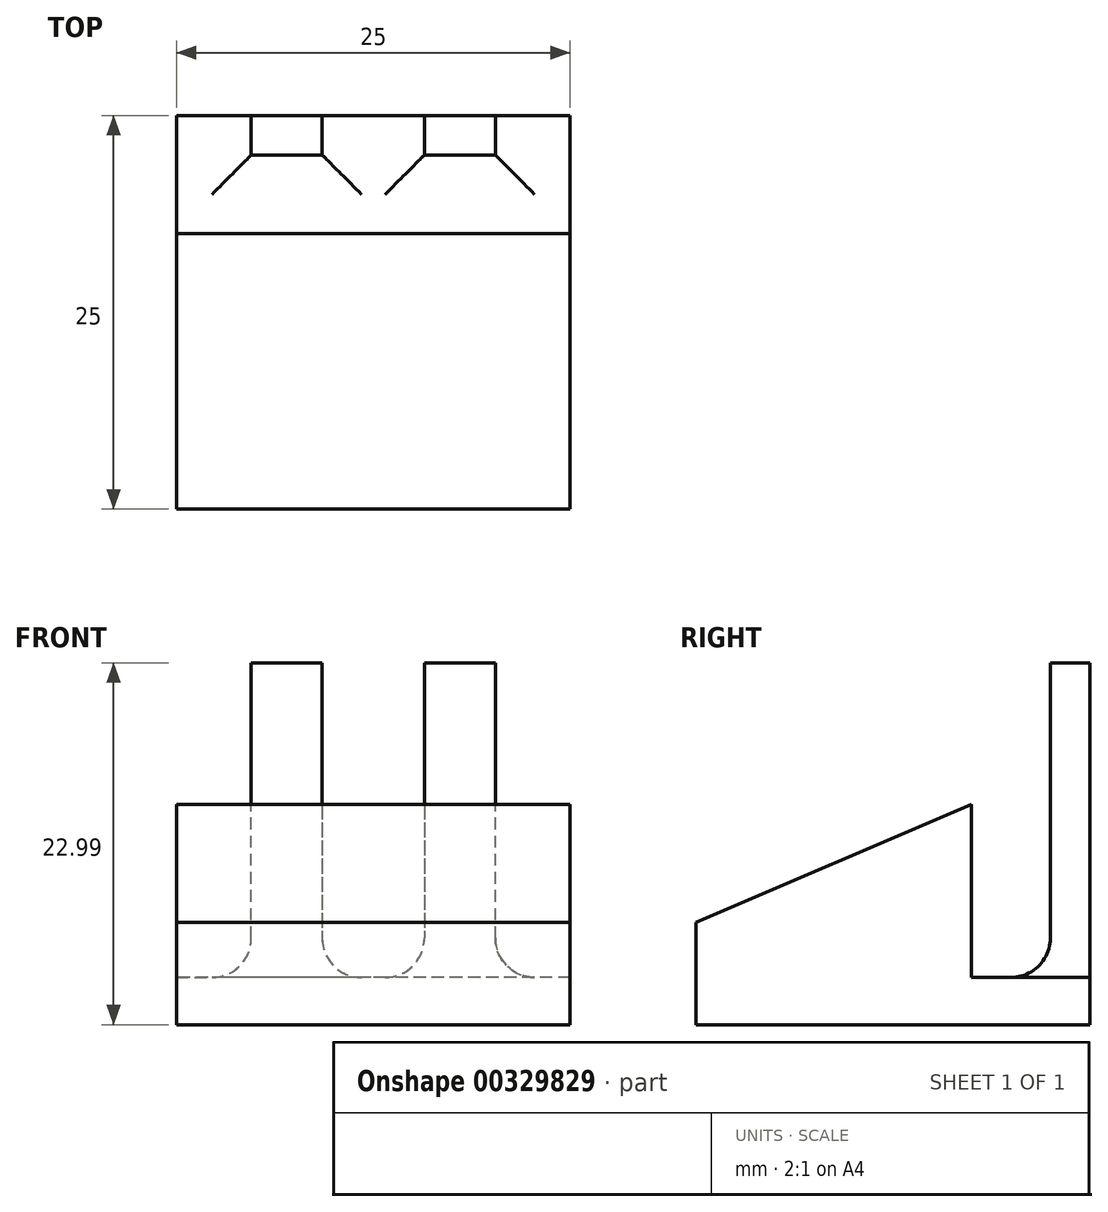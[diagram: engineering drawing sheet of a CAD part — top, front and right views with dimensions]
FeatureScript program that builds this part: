
annotation { "Feature Type Name" : "Feature", "Feature Type Description" : "" }
export const myFeature = defineFeature(function(context is Context, id is Id, definition is map)
    precondition{}
    {
        {
            var Q0;
            Q0=qCreatedBy(makeId("Right.planeOp"),FACE);
            var sketch = newSketch(context, id + "F0", { "sketchPlane" : qUnion([Q0])});
            skLineSegment(sketch, "E0", {"start": v(0, 23) * mm, "end": v(0, 0) * mm});
            skLineSegment(sketch, "E1", {"start": v(0, 0) * mm, "end": v(0, 0) * mm});
            skLineSegment(sketch, "E2", {"start": v(-25, 0) * mm, "end": v(-25, 0) * mm});
            skLineSegment(sketch, "E3", {"start": v(-25, 0) * mm, "end": v(-25, 6.5) * mm});
            skLineSegment(sketch, "E4", {"start": v(-25, 6.5) * mm, "end": v(-7.5, 14) * mm});
            skLineSegment(sketch, "E5", {"start": v(-7.5, 14) * mm, "end": v(-7.5, 14) * mm});
            skLineSegment(sketch, "E6", {"start": v(-7.5, 3) * mm, "end": v(-7.5, 3) * mm});
            skLineSegment(sketch, "E7", {"start": v(-7.5, 3) * mm, "end": v(-7.5, 14) * mm});
            skLineSegment(sketch, "E8", {"start": v(-7.5, 3) * mm, "end": v(-2.5, 3) * mm});
            skLineSegment(sketch, "E9", {"start": v(-2.5, 3) * mm, "end": v(-2.5, 3) * mm});
            skLineSegment(sketch, "E10", {"start": v(-2.5, 3) * mm, "end": v(-2.5, 23) * mm});
            skLineSegment(sketch, "E11", {"start": v(-2.5, 23) * mm, "end": v(-2.5, 23) * mm});
            skLineSegment(sketch, "E12", {"start": v(-2.5, 23) * mm, "end": v(0, 23) * mm});
            skLineSegment(sketch, "E13", {"start": v(-25, 0) * mm, "end": v(0, 0) * mm});
            skLineSegment(sketch, "E14", {"start": v(0, 60) * mm, "end": v(-140, 0) * mm, "construction": true});
            skSolve(sketch);
        }
        {
            var Q0;
            Q0 = qSketchRegion(id + "F0", true);
            extrude(context, id + "F1", {"entities" : qUnion([Q0]), "depth" : 25 * mm});
        }
        {
            var Q0;
            Q0=makeQuery(id+"F1.opExtrude","SWEPT_FACE",FACE,{"disambiguationData":[OSD([sQuery(id+"F0.wireOp",EDGE,"E0")])]});
            var sketch = newSketch(context, id + "F2", { "sketchPlane" : qUnion([Q0])});
            skLineSegment(sketch, "E15", {"start": v(-25, 3) * mm, "end": v(-20.25, 3) * mm});
            skLineSegment(sketch, "E16", {"start": v(-20.25, 3) * mm, "end": v(-20.25, 22.99) * mm});
            skLineSegment(sketch, "E17", {"start": v(-20.25, 22.99) * mm, "end": v(-15.75, 22.99) * mm});
            skLineSegment(sketch, "E18", {"start": v(-15.75, 22.99) * mm, "end": v(-15.75, 3) * mm});
            skLineSegment(sketch, "E19", {"start": v(-15.75, 3) * mm, "end": v(-12.5, 3) * mm});
            skLineSegment(sketch, "E20", {"start": v(-12.5, 23) * mm, "end": v(-12.5, 0) * mm, "construction": true});
            skLineSegment(sketch, "E21.MirrorCS", {"start": v(-9.25, 3) * mm, "end": v(-12.5, 3) * mm});
            skLineSegment(sketch, "E22.MirrorCS", {"start": v(-9.25, 22.99) * mm, "end": v(-9.25, 3) * mm});
            skLineSegment(sketch, "E23.MirrorCS", {"start": v(-4.75, 3) * mm, "end": v(-4.75, 22.99) * mm});
            skLineSegment(sketch, "E24.MirrorCS", {"start": v(0, 3) * mm, "end": v(-4.75, 3) * mm});
            skLineSegment(sketch, "E25.MirrorCS", {"start": v(-4.75, 22.99) * mm, "end": v(-9.25, 22.99) * mm});
            skLineSegment(sketch, "E26", {"start": v(-25, 3) * mm, "end": v(-25, 23) * mm});
            skLineSegment(sketch, "E27", {"start": v(-25, 23) * mm, "end": v(0, 23) * mm});
            skLineSegment(sketch, "E28", {"start": v(0, 23) * mm, "end": v(0, 3) * mm});
            skSolve(sketch);
        }
        {
            var Q0;
            Q0 = qSketchRegion(id + "F2", true);
            extrude(context, id + "F3", {"entities" : qUnion([Q0]), "operationType" : NewBodyOperationType.REMOVE, "endBound" : BoundingType.UP_TO_NEXT, "oppositeDirection" : true, "depth" : 25 * mm});
        }
        {
            var Q0;
            Q0=makeQuery(id+"F3.boolean.opBoolean","COPY",EDGE,{"derivedFrom":makeQuery(id+"F3.opExtrude","SWEPT_EDGE",EDGE,{"disambiguationData":[OSD([sQuery(id+"F2.wireOp",EDGE,"E15"),sQuery(id+"F2.wireOp",EDGE,"E16")])]})});
            var Q1;
            {var subQ0=sQuery(id+"F0.wireOp",EDGE,"E10");var subQ1=sQuery(id+"F0.wireOp",EDGE,"E8");Q1=makeQuery(id+"F3.boolean.opBoolean","SPLIT",EDGE,{"disambiguationData":[TD([makeQuery(id+"F3.opExtrude","SWEPT_FACE",FACE,{"disambiguationData":[OSD([sQuery(id+"F2.wireOp",EDGE,"E16")])]})])],"derivedFrom":makeQuery(id+"F1.opExtrude","SWEPT_EDGE",EDGE,{"disambiguationData":[OSD([subQ1,subQ0])]})});}
            var Q2;
            Q2=makeQuery(id+"F3.boolean.opBoolean","COPY",EDGE,{"derivedFrom":makeQuery(id+"F3.opExtrude","SWEPT_EDGE",EDGE,{"disambiguationData":[OSD([sQuery(id+"F2.wireOp",EDGE,"E21.MirrorCS"),sQuery(id+"F2.wireOp",EDGE,"E22.MirrorCS")])]})});
            var Q3;
            Q3=makeQuery(id+"F3.boolean.opBoolean","COPY",EDGE,{"derivedFrom":makeQuery(id+"F3.opExtrude","SWEPT_EDGE",EDGE,{"disambiguationData":[OSD([sQuery(id+"F2.wireOp",EDGE,"E18"),sQuery(id+"F2.wireOp",EDGE,"E19")])]})});
            var Q4;
            Q4=makeQuery(id+"F3.boolean.opBoolean","COPY",EDGE,{"derivedFrom":makeQuery(id+"F3.opExtrude","SWEPT_EDGE",EDGE,{"disambiguationData":[OSD([sQuery(id+"F2.wireOp",EDGE,"E23.MirrorCS"),sQuery(id+"F2.wireOp",EDGE,"E24.MirrorCS")])]})});
            var Q5;
            {var subQ0=sQuery(id+"F0.wireOp",EDGE,"E10");var subQ1=sQuery(id+"F0.wireOp",EDGE,"E8");Q5=makeQuery(id+"F3.boolean.opBoolean","SPLIT",EDGE,{"disambiguationData":[TD([makeQuery(id+"F3.opExtrude","SWEPT_FACE",FACE,{"disambiguationData":[OSD([sQuery(id+"F2.wireOp",EDGE,"E22.MirrorCS")])]})])],"derivedFrom":makeQuery(id+"F1.opExtrude","SWEPT_EDGE",EDGE,{"disambiguationData":[OSD([subQ1,subQ0])]})});}
            fillet(context, id + "F4", {"entities" : qUnion([Q0, Q1, Q2, Q3, Q4, Q5]), "radius" : 2.5 * mm, "tangentPropagation" : true, "allowEdgeOverflow" : false});
        }
    });
